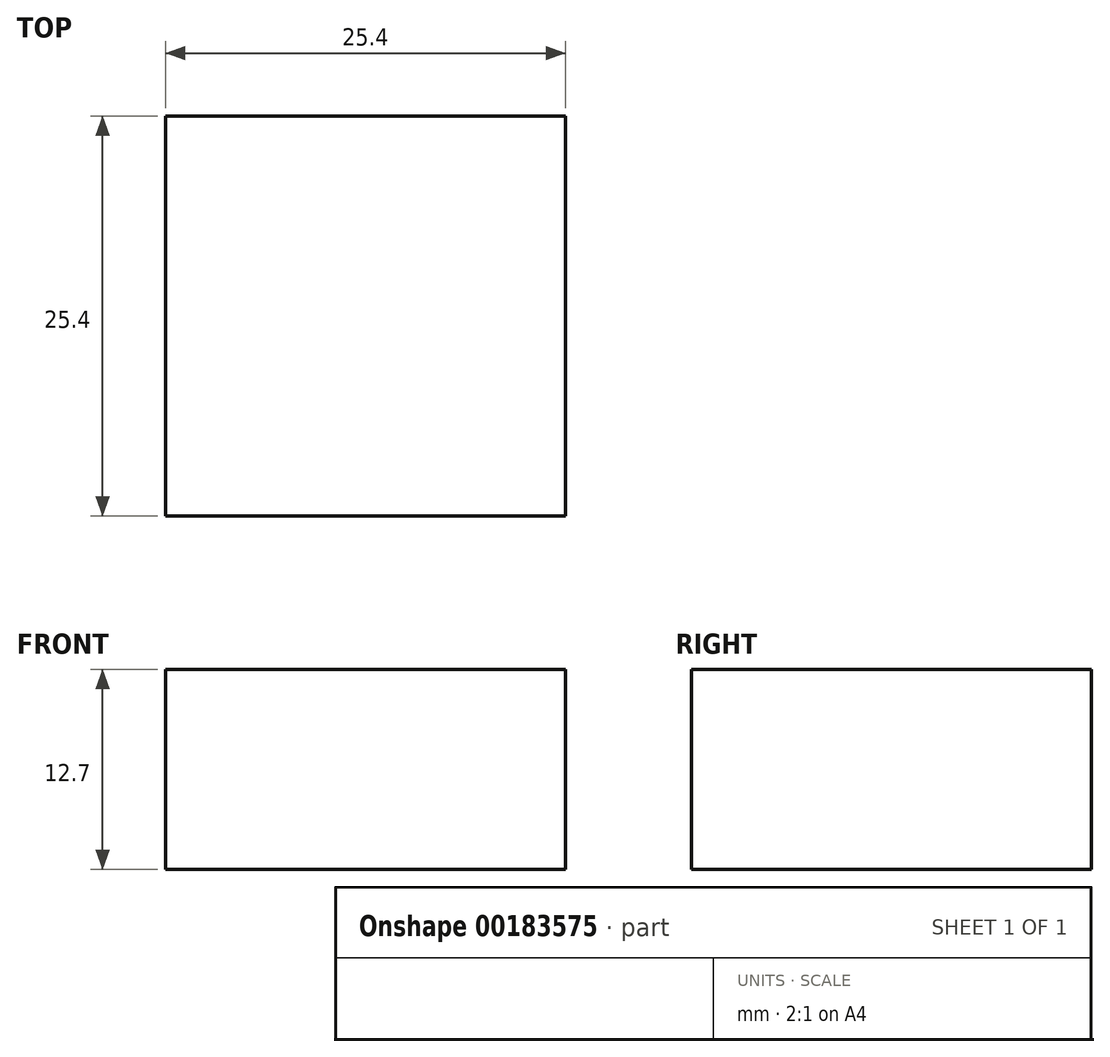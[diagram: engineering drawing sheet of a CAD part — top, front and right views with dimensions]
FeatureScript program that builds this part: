
annotation { "Feature Type Name" : "Feature", "Feature Type Description" : "" }
export const myFeature = defineFeature(function(context is Context, id is Id, definition is map)
    precondition{}
    {
        {
            var Q0;
            Q0=qCreatedBy(makeId("Top.planeOp"),FACE);
            var sketch = newSketch(context, id + "F0", { "sketchPlane" : qUnion([Q0])});
            skLineSegment(sketch, "E0.bottom", {"start": v(12.7, 12.7) * mm, "end": v(-12.7, 12.7) * mm});
            skLineSegment(sketch, "E0.top", {"start": v(12.7, -12.7) * mm, "end": v(-12.7, -12.7) * mm});
            skLineSegment(sketch, "E0.left", {"start": v(12.7, 12.7) * mm, "end": v(12.7, -12.7) * mm});
            skLineSegment(sketch, "E0.right", {"start": v(-12.7, 12.7) * mm, "end": v(-12.7, -12.7) * mm});
            skPoint(sketch, "E0.middle", {"position": v(0, 0) * mm});
            skSolve(sketch);
        }
        {
            var Q0;
            Q0 = qSketchRegion(id + "F0", true);
            extrude(context, id + "F1", {"entities" : qUnion([Q0]), "depth" : 12.7 * mm});
        }
    });
